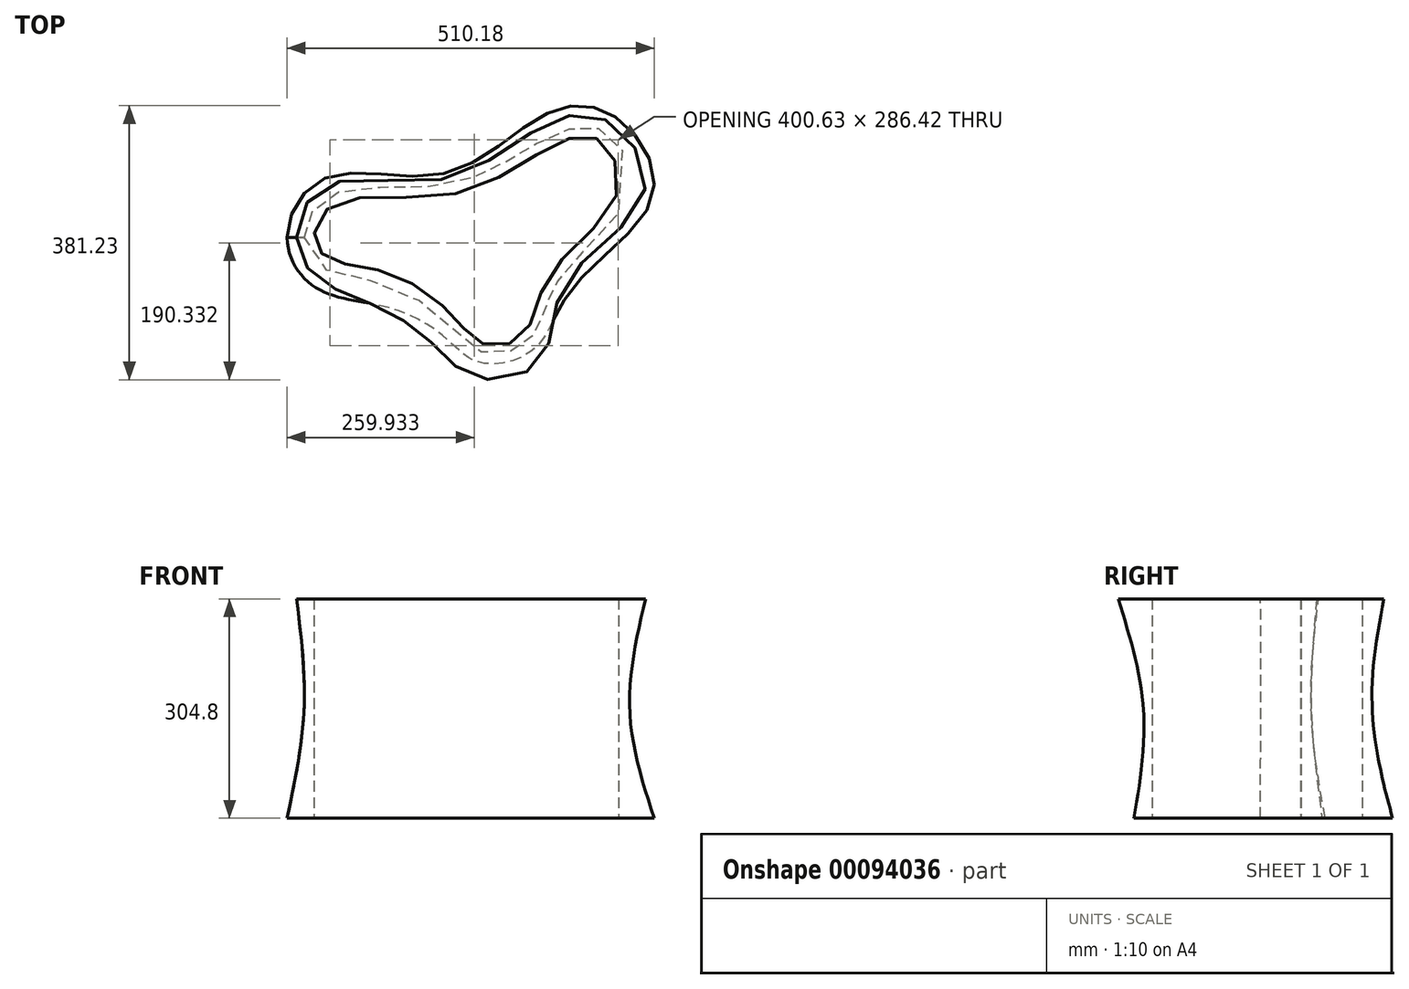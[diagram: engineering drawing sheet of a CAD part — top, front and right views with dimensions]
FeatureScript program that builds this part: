
annotation { "Feature Type Name" : "Feature", "Feature Type Description" : "" }
export const myFeature = defineFeature(function(context is Context, id is Id, definition is map)
    precondition{}
    {
        {
            var Q0;
            Q0=qCreatedBy(makeId("Top.planeOp"),FACE);
            var sketch = newSketch(context, id + "F0", { "sketchPlane" : qUnion([Q0])});
            skFitSpline(sketch, "E0", {"points": [v(-303.8, 0) * mm, v(-248.3, 83.96) * mm, v(-83.24, 89.65) * mm, v(59.05, 173.6) * mm, v(154.4, 166.49) * mm, v(204.2, 58.34) * mm, v(93.2, -69.73) * mm, v(40.55, -153.68) * mm, v(-36.29, -173.6) * mm, v(-88.94, -135.18) * mm, v(-170.04, -95.34) * mm, v(-261.11, -71.15) * mm, v(-303.8, 0) * mm]});
            skSolve(sketch);
        }
        {
            var Q0;
            Q0=qCreatedBy(makeId("Top.planeOp"),FACE);
            cPlane(context, id + "F1", {"entities" : qUnion([Q0]), "cplaneType" : CPlaneType.OFFSET, "offset" : 152.4 * mm, "width" : 152.4 * mm, "height" : 152.4 * mm});
        }
        {
            var Q0;
            Q0=qCreatedBy(id+"F1.planeOp",FACE);
            var sketch = newSketch(context, id + "F2", { "sketchPlane" : qUnion([Q0])});
            skFitSpline(sketch, "E1", {"points": [v(-74, 75.76) * mm, v(-240.15, 60.87) * mm, v(-280.26, 0) * mm, v(-250.46, -44.56) * mm, v(-166.81, -65.18) * mm, v(-79.72, -121.33) * mm, v(-33.89, -160.3) * mm, v(31.43, -144.25) * mm, v(73.83, -58.3) * mm, v(168.94, 57.43) * mm, v(140.3, 146.81) * mm, v(63.52, 142.23) * mm, v(-74, 75.76) * mm]});
            skSolve(sketch);
        }
        {
            var Q0;
            Q0=qCreatedBy(id+"F1.planeOp",FACE);
            cPlane(context, id + "F3", {"entities" : qUnion([Q0]), "cplaneType" : CPlaneType.OFFSET, "offset" : 152.4 * mm, "width" : 152.4 * mm, "height" : 152.4 * mm});
        }
        {
            var Q0;
            Q0=qCreatedBy(id+"F3.planeOp",FACE);
            var sketch = newSketch(context, id + "F4", { "sketchPlane" : qUnion([Q0])});
            skFitSpline(sketch, "E2", {"points": [v(-40.25, -194.78) * mm, v(-101.75, -147.55) * mm, v(-170.38, -99.42) * mm, v(-255.95, -60.2) * mm, v(-290.71, 0) * mm, v(-247.04, 73.5) * mm, v(-82.14, 82.41) * mm, v(61.36, 160.85) * mm, v(148.7, 158.17) * mm, v(191.49, 58.35) * mm, v(81.86, -64.65) * mm, v(48.88, -169.83) * mm, v(-40.25, -194.78) * mm]});
            skSolve(sketch);
        }
        {
            var Q0;
            Q0 = qSketchRegion(id + "F0", true);
            var Q1;
            Q1 = qSketchRegion(id + "F2", true);
            var Q2;
            Q2 = qSketchRegion(id + "F4", true);
            loft(context, id + "F5", {"sheetProfilesArray" : [{ "sheetProfileEntities" : qUnion([Q0]) }, { "sheetProfileEntities" : qUnion([Q1]) }, { "sheetProfileEntities" : qUnion([Q2]) }]});
        }
        {
            var Q0;
            Q0=makeQuery(id+"F5.opLoft","CAP_FACE",FACE,{"disambiguationData":[OSD([makeQuery(id+"F4.imprint","IMPRINT",FACE,{"disambiguationData":[TD([[makeQuery(id+"F4.imprint","IMPRINT",EDGE,{"derivedFrom":sQuery(id+"F4.wireOp",EDGE,"E2")}),-1.0]])]})])],"isStart":true});
            var sketch = newSketch(context, id + "F6", { "sketchPlane" : qUnion([Q0])});
            skFitSpline(sketch, "E3", {"points": [v(-69.78, 61.04) * mm, v(-235.2, 48.48) * mm, v(-266.2, 0) * mm, v(-242.58, -30.53) * mm, v(-160.6, -49.73) * mm, v(-72, -110.29) * mm, v(-30.64, -147.95) * mm, v(24, -135.4) * mm, v(60.93, -51.95) * mm, v(153.24, 57.34) * mm, v(132.56, 134.14) * mm, v(68.31, 129.71) * mm, v(-69.78, 61.04) * mm]});
            skSolve(sketch);
        }
        {
            var Q0;
            Q0 = qSketchRegion(id + "F6", true);
            extrude(context, id + "F7", {"entities" : qUnion([Q0]), "operationType" : NewBodyOperationType.REMOVE, "endBound" : BoundingType.THROUGH_ALL, "oppositeDirection" : true, "depth" : 25.4 * mm});
        }
    });
